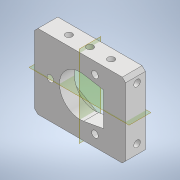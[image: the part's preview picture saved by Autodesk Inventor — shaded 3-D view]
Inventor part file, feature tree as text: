
AUTODESK INVENTOR PART (.ipt)
format: ipt  version: 2022 (Build 260153000, 153)  size: 202,240 bytes
history: native  units: mm
features: sketch x4, hole x4, extrude x2, plane x2, mirror x1, chamfer x1, thicken_offset x1, projected_geometry x1
ambient origin geometry x8: Origin, YZ Plane, XZ Plane, XY Plane, X Axis, Y Axis, Z Axis, Center Point
bodies: Solid1 (feature_tree)
feature tree (16):
  sketch  "Sketch1"  dims[d0=24.5mm d1=45.0mm]
  extrude  "Extrusion1"  Depth=45.0mm
  extrude  "Extrusion2"  Depth=55.0mm
  hole  "Hole1"  [1 undecoded]
  plane  "Work Plane1"
  hole  "Hole2"  [1 undecoded]
  hole  "Hole3"  [1 undecoded]
  plane  "Work Plane2"
  mirror  "Mirror2"
  chamfer  "Chamfer1"  Distance=2.0mm
  hole  "Hole4"  [1 undecoded]
  thicken_offset  "Thicken1"
  sketch  "Sketch3"  dims[d2=55.0mm d3=14.0mm]
  sketch  "Sketch4"  dims[d4=12.0mm d5=0.0mm d7=16.0mm]
  projected_geometry  "Projected Loop1"
  sketch  "Sketch5"  dims[d9=6.0mm d10=3.0mm d11=0.0mm d12=4.0mm d13=6.0mm d14=6.3mm d15=2.0mm d16=90.0deg d17=8.0mm d18=20.594885mm d24=4.0mm d25=6.0mm d26=4.0mm d27=2.0mm d28=90.0deg d29=8.0mm d30=20.594885mm d31=2.0mm d32=2.0mm d33=2.0mm d35=12.75mm d36=12.75mm d37=12.75mm d38=4.0mm d39=6.0mm d40=4.0mm d41=2.0mm d42=90.0deg d43=5.0mm d44=0.0mm d45=2.0mm d46=2.0mm d47=45.0deg d48=4.0mm d49=6.0mm d50=6.3mm d51=2.0mm d52=90.0deg d53=8.0mm d54=0.0mm d55=0.2mm d56=0.2mm d57=13.962634mm]
note: 4 required parameter values undecoded (feature->parameter linkage not recoverable at this tier; creation-order binding heuristic only, values carry confidence <= 0.55)
